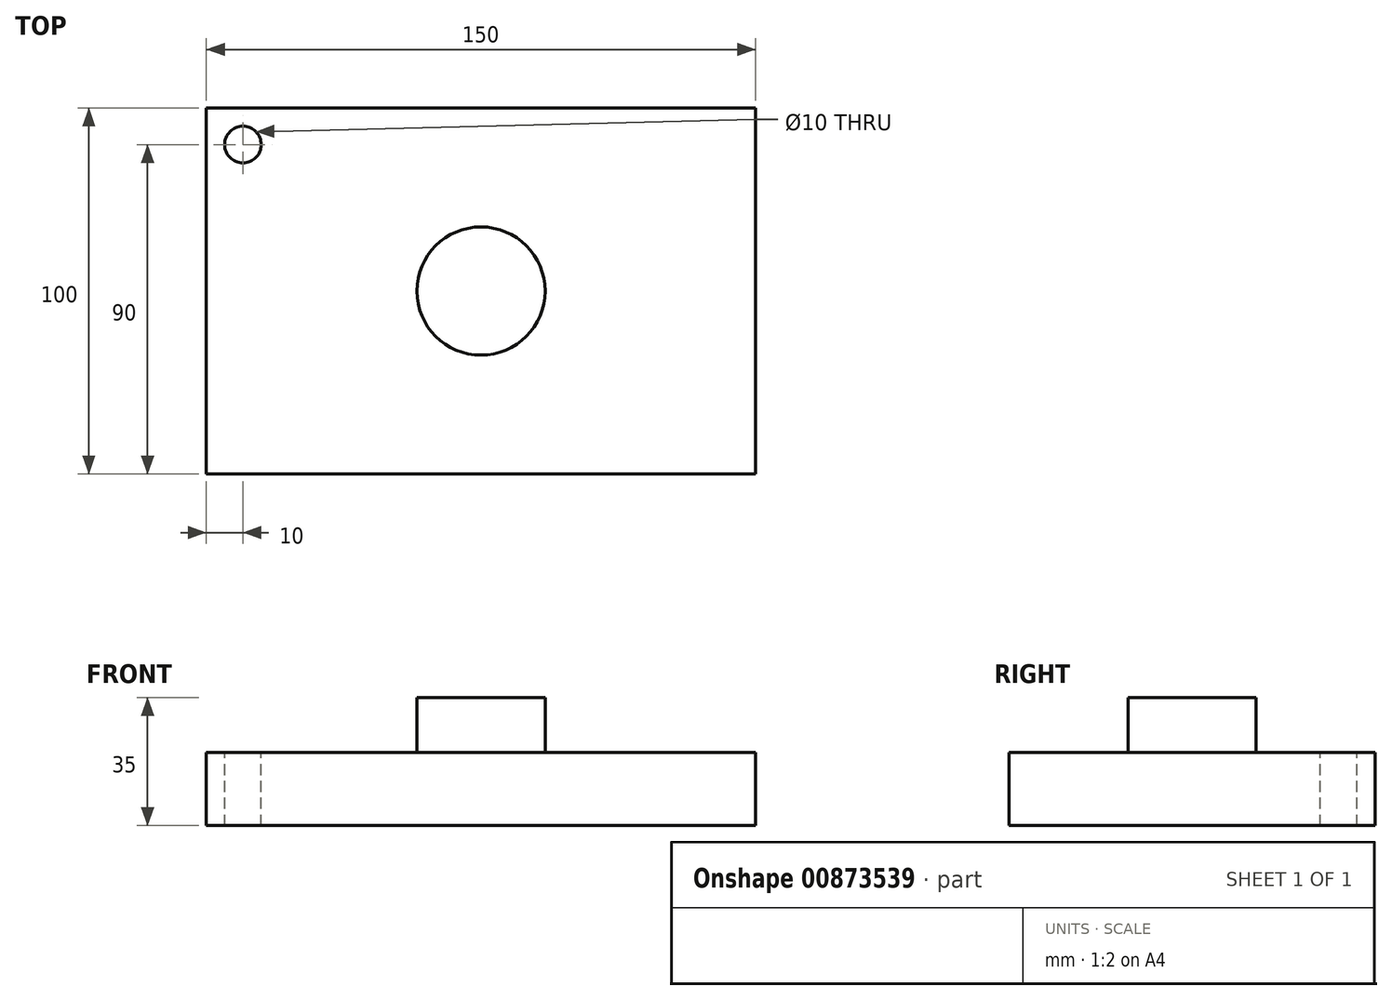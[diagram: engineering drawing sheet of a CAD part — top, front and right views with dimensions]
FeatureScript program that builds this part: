
annotation { "Feature Type Name" : "Feature", "Feature Type Description" : "" }
export const myFeature = defineFeature(function(context is Context, id is Id, definition is map)
    precondition{}
    {
        {
            var Q0;
            Q0=qCreatedBy(makeId("Top.planeOp"),FACE);
            var sketch = newSketch(context, id + "F0", { "sketchPlane" : qUnion([Q0])});
            skLineSegment(sketch, "E0.bottom", {"start": v(75, -50) * mm, "end": v(-75, -50) * mm});
            skLineSegment(sketch, "E0.top", {"start": v(75, 50) * mm, "end": v(-75, 50) * mm});
            skLineSegment(sketch, "E0.left", {"start": v(75, -50) * mm, "end": v(75, 50) * mm});
            skLineSegment(sketch, "E0.right", {"start": v(-75, -50) * mm, "end": v(-75, 50) * mm});
            skPoint(sketch, "E0.middle", {"position": v(0, 0) * mm});
            skSolve(sketch);
        }
        {
            var Q0;
            Q0 = qSketchRegion(id + "F0", true);
            extrude(context, id + "F1", {"entities" : qUnion([Q0]), "depth" : 20 * mm, "offsetDistance" : 25 * mm});
        }
        {
            var Q0;
            Q0=makeQuery(id+"F1.opExtrude","CAP_FACE",FACE,{"disambiguationData":[OSD([sQuery(id+"F0.wireOp",EDGE,"E0.bottom"),sQuery(id+"F0.wireOp",EDGE,"E0.top"),sQuery(id+"F0.wireOp",EDGE,"E0.left"),sQuery(id+"F0.wireOp",EDGE,"E0.right")])],"isStart":false});
            var sketch = newSketch(context, id + "F2", { "sketchPlane" : qUnion([Q0])});
            skCircle(sketch, "E1", {"center": v(0, 0) * mm, "radius": 17.5 * mm});
            skSolve(sketch);
        }
        {
            var Q0;
            Q0 = qSketchRegion(id + "F2", true);
            extrude(context, id + "F3", {"entities" : qUnion([Q0]), "operationType" : NewBodyOperationType.ADD, "depth" : 15 * mm, "offsetDistance" : 25 * mm});
        }
        {
            var Q0;
            Q0=makeQuery(id+"F1.opExtrude","CAP_FACE",FACE,{"disambiguationData":[OSD([sQuery(id+"F0.wireOp",EDGE,"E0.bottom"),sQuery(id+"F0.wireOp",EDGE,"E0.top"),sQuery(id+"F0.wireOp",EDGE,"E0.left"),sQuery(id+"F0.wireOp",EDGE,"E0.right")])],"isStart":false});
            var sketch = newSketch(context, id + "F4", { "sketchPlane" : qUnion([Q0])});
            skPoint(sketch, "E2", {"position": v(-65, 40) * mm});
            skSolve(sketch);
        }
        {
            var Q0;
            Q0=sQuery(id+"F4.wireOp",VERTEX,"E2");
            var Q1;
            Q1=makeQuery(id+"F1.opExtrude","SWEPT_BODY",BODY,{"disambiguationData":[OSD([sQuery(id+"F0.wireOp",EDGE,"E0.bottom"),sQuery(id+"F0.wireOp",EDGE,"E0.top"),sQuery(id+"F0.wireOp",EDGE,"E0.left"),sQuery(id+"F0.wireOp",EDGE,"E0.right")])]});
            hole(context, id + "F5", {"style" : HoleStyle.SIMPLE, "endStyle" : HoleEndStyle.THROUGH, "holeDiameter" : 10 * mm, "majorDiameter" : 5 * mm, "isTappedThrough" : true, "tappedDepth" : 12 * mm, "tapClearance" : 3, "locations" : qUnion([Q0]), "scope" : qUnion([Q1])});
        }
    });
